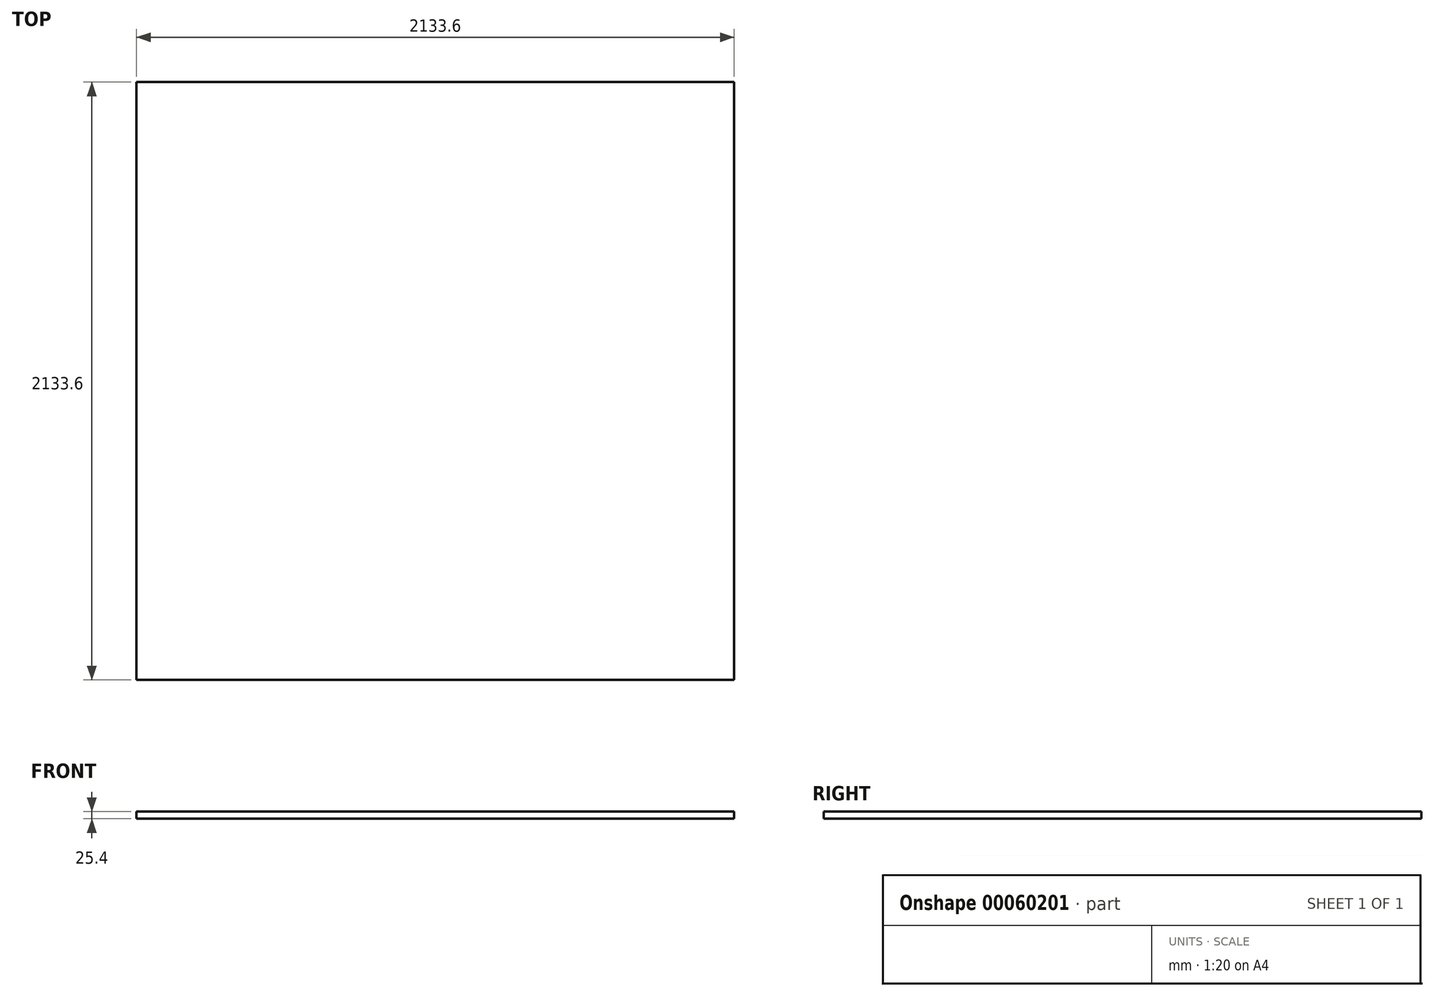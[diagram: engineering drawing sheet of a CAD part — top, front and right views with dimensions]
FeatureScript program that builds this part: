
annotation { "Feature Type Name" : "Feature", "Feature Type Description" : "" }
export const myFeature = defineFeature(function(context is Context, id is Id, definition is map)
    precondition{}
    {
        {
            var Q0;
            Q0=qCreatedBy(makeId("Top.planeOp"),FACE);
            var sketch = newSketch(context, id + "F0", { "sketchPlane" : qUnion([Q0])});
            skLineSegment(sketch, "E0.rect.bottom", {"start": v(1066.8, 1066.8) * mm, "end": v(-1066.8, 1066.8) * mm});
            skLineSegment(sketch, "E0.rect.top", {"start": v(1066.8, -1066.8) * mm, "end": v(-1066.8, -1066.8) * mm});
            skLineSegment(sketch, "E0.rect.left", {"start": v(1066.8, 1066.8) * mm, "end": v(1066.8, -1066.8) * mm});
            skLineSegment(sketch, "E0.rect.right", {"start": v(-1066.8, 1066.8) * mm, "end": v(-1066.8, -1066.8) * mm});
            skPoint(sketch, "E0.rect.middle", {"position": v(0, 0) * mm});
            skSolve(sketch);
        }
        {
            var Q0;
            Q0=makeQuery(id+"F0.imprint","IMPRINT",FACE,{"disambiguationData":[TD([[makeQuery(id+"F0.imprint","IMPRINT",EDGE,{"derivedFrom":sQuery(id+"F0.wireOp",EDGE,"E0.rect.bottom")}),1.0]])]});
            extrude(context, id + "F1", {"entities" : qUnion([Q0]), "depth" : 25.4 * mm});
        }
    });
